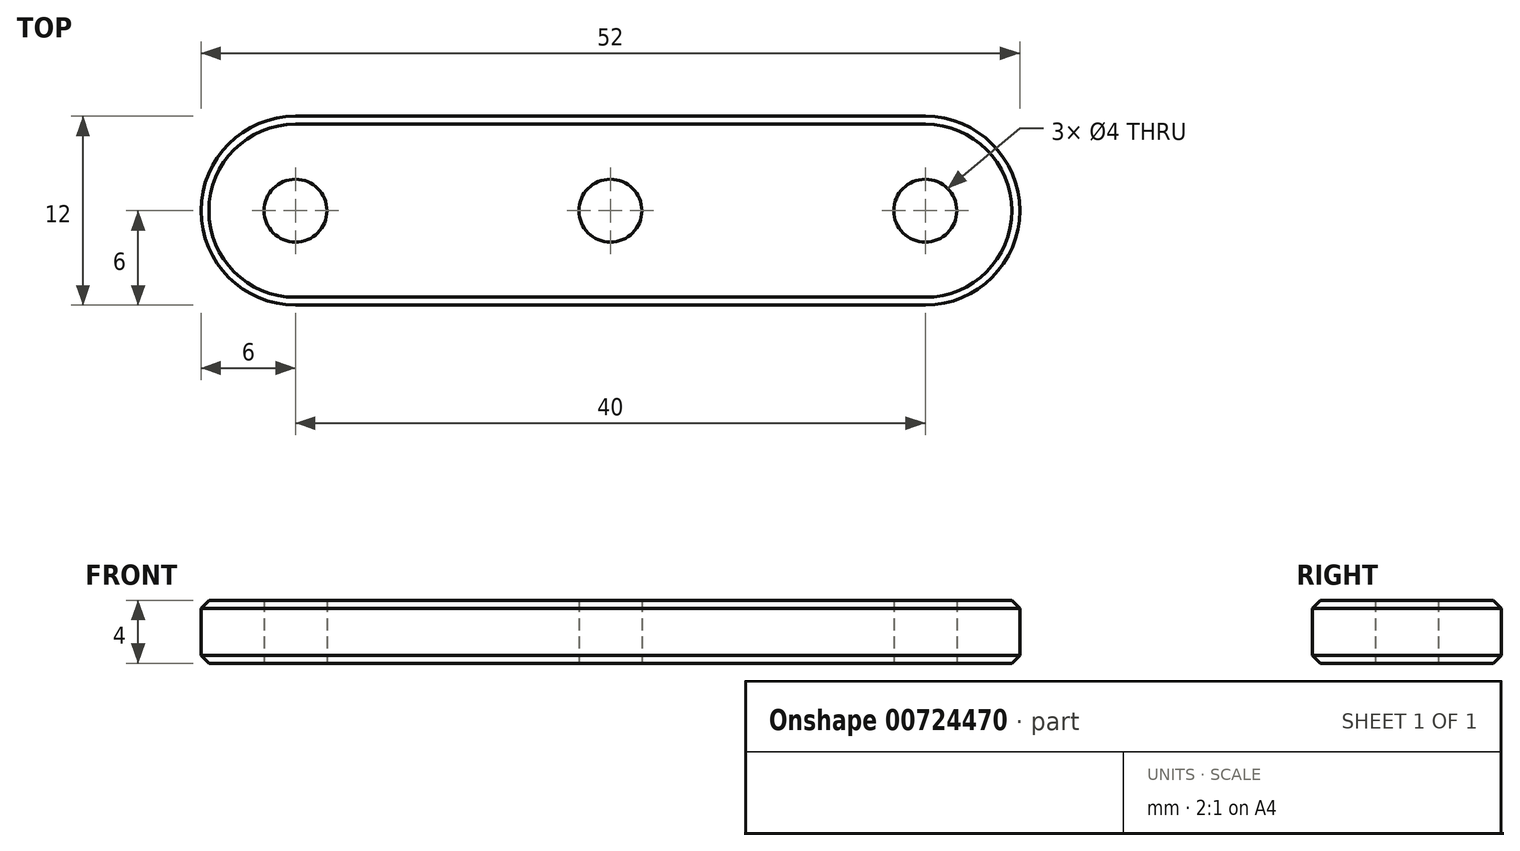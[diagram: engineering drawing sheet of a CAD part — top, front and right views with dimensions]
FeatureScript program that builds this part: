
annotation { "Feature Type Name" : "Feature", "Feature Type Description" : "" }
export const myFeature = defineFeature(function(context is Context, id is Id, definition is map)
    precondition{}
    {
        {
            var Q0;
            Q0=qCreatedBy(makeId("Top.planeOp"),FACE);
            var sketch = newSketch(context, id + "F0", { "sketchPlane" : qUnion([Q0])});
            skCircle(sketch, "E0", {"center": v(0, 0) * mm, "radius": 2 * mm});
            skCircle(sketch, "E1", {"center": v(20, 0) * mm, "radius": 2 * mm});
            skCircle(sketch, "E2", {"center": v(-20, 0) * mm, "radius": 2 * mm});
            skArc(sketch, "E3", {"start": v(-20, 6) * mm, "mid": v(-26, 0) * mm, "end": v(-20, -6) * mm});
            skArc(sketch, "E4", {"start": v(20, -6) * mm, "mid": v(26, 0) * mm, "end": v(20, 6) * mm});
            skLineSegment(sketch, "E5", {"start": v(-20, 6) * mm, "end": v(20, 6) * mm});
            skLineSegment(sketch, "E6", {"start": v(20, -6) * mm, "end": v(-20, -6) * mm});
            skSolve(sketch);
        }
        {
            var Q0;
            Q0=makeQuery(id+"F0.imprint","IMPRINT",FACE,{"disambiguationData":[TD([[makeQuery(id+"F0.imprint","IMPRINT",EDGE,{"derivedFrom":sQuery(id+"F0.wireOp",EDGE,"E0")}),-1.0]])]});
            extrude(context, id + "F1", {"entities" : qUnion([Q0]), "depth" : 4 * mm, "offsetDistance" : 25 * mm});
        }
        {
            var Q0;
            Q0=makeQuery(id+"F1.opExtrude","CAP_EDGE",EDGE,{"disambiguationData":[OSD([sQuery(id+"F0.wireOp",EDGE,"E3")])],"isStart":false});
            var Q1;
            Q1=makeQuery(id+"F1.opExtrude","CAP_EDGE",EDGE,{"disambiguationData":[OSD([sQuery(id+"F0.wireOp",EDGE,"E4")])],"isStart":true});
            chamfer(context, id + "F2", {"entities" : qUnion([Q0, Q1]), "width" : 0.5 * mm, "tangentPropagation" : true});
        }
    });
